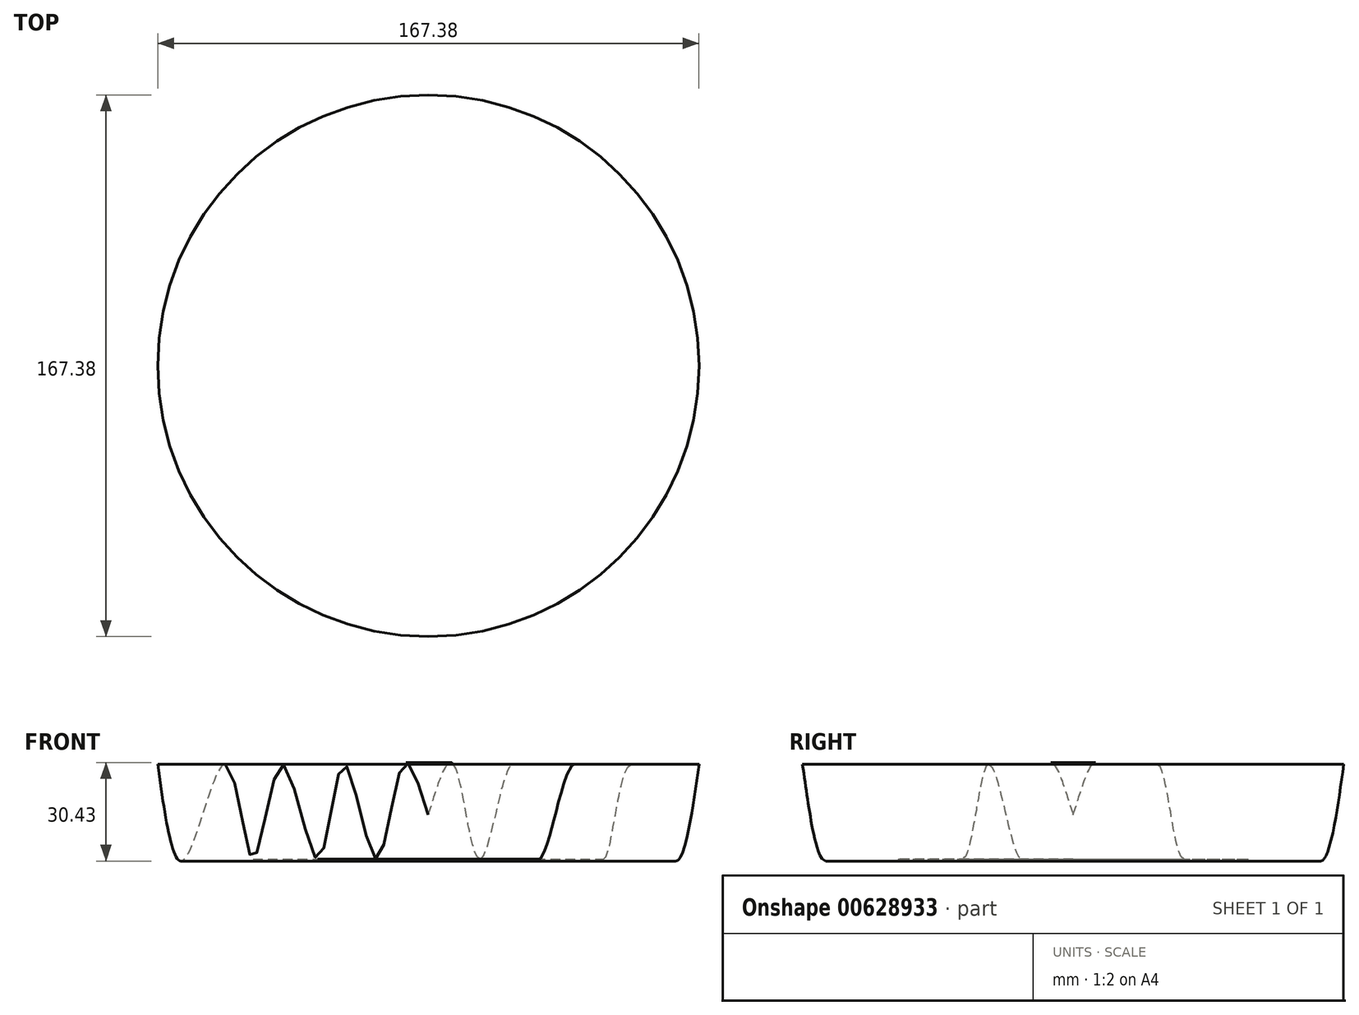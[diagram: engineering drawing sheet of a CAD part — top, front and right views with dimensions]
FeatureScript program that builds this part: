
annotation { "Feature Type Name" : "Feature", "Feature Type Description" : "" }
export const myFeature = defineFeature(function(context is Context, id is Id, definition is map)
    precondition{}
    {
        {
            var Q0;
            Q0=qCreatedBy(makeId("Front.planeOp"),FACE);
            var sketch = newSketch(context, id + "F0", { "sketchPlane" : qUnion([Q0])});
            skFitSpline(sketch, "E0", {"points": [v(0, 0) * mm, v(-7.82, 15.59) * mm, v(-16.12, -13.69) * mm, v(-26.12, 15.59) * mm, v(-34.17, -13.69) * mm, v(-45.15, 15.59) * mm, v(-54.18, -13.69) * mm, v(-62.47, 15.59) * mm, v(-75.4, -13.69) * mm, v(-83.7, 15.59) * mm], "startDerivative": vector(-98.99, 306.32) * mm, "endDerivative": vector(-61.24, 423.48) * mm});
            skLineSegment(sketch, "E1", {"start": v(-97.84, 15.59) * mm, "end": v(32.92, 15.59) * mm, "construction": true});
            skLineSegment(sketch, "E2", {"start": v(-98.58, -13.69) * mm, "end": v(32.92, -13.69) * mm, "construction": true});
            skSolve(sketch);
        }
        {
            var Q0;
            Q0=qCreatedBy(makeId("Front.planeOp"),FACE);
            var sketch = newSketch(context, id + "F1", { "sketchPlane" : qUnion([Q0])});
            skLineSegment(sketch, "E3", {"start": v(0, -56.87) * mm, "end": v(0, 59.74) * mm, "construction": true});
            skSolve(sketch);
        }
        {
            var Q0;
            Q0 = qSketchRegion(id + "F0", true);
            var Q1;
            Q1 = qConstructionFilter(qBodyType(qCreatedBy(id + "F0" ,EDGE), BodyType.WIRE), ConstructionObject.NO);
            var Q2;
            Q2=sQuery(id+"F1.wireOp",EDGE,"E3");
            revolve(context, id + "F2", {"bodyType" : ToolBodyType.SURFACE, "entities" : qUnion([Q0]), "surfaceEntities" : qUnion([Q1]), "axis" : qUnion([Q2]), "revolveType" : RevolveType.FULL});
        }
    });
